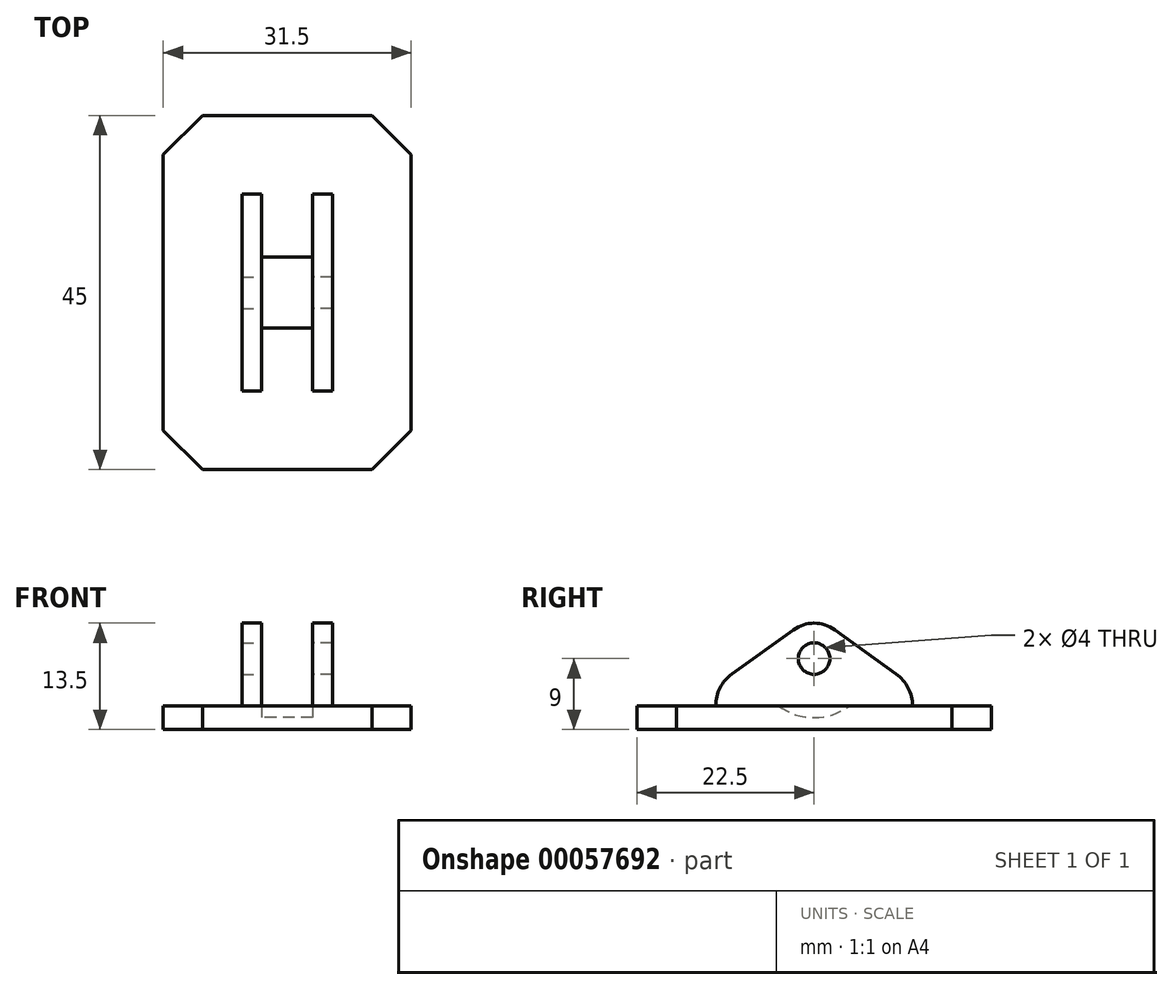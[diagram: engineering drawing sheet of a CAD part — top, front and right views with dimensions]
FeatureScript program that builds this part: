
annotation { "Feature Type Name" : "Feature", "Feature Type Description" : "" }
export const myFeature = defineFeature(function(context is Context, id is Id, definition is map)
    precondition{}
    {
        {
            var Q0;
            Q0=qCreatedBy(makeId("Right.planeOp"),FACE);
            var sketch = newSketch(context, id + "F0", { "sketchPlane" : qUnion([Q0])});
            skLineSegment(sketch, "E0", {"start": v(0, 0) * mm, "end": v(0, 6) * mm, "construction": true});
            skCircle(sketch, "E1", {"center": v(0, 6) * mm, "radius": 6.5 * mm, "construction": true});
            skCircle(sketch, "E2", {"center": v(0, 6) * mm, "radius": 2 * mm, "construction": true});
            skCircle(sketch, "E3", {"center": v(0, 6) * mm, "radius": 4.5 * mm, "construction": true});
            skLineSegment(sketch, "E4", {"start": v(-12.5, 0) * mm, "end": v(12.5, 0) * mm, "construction": true});
            skLineSegment(sketch, "E5", {"start": v(-12.5, -3) * mm, "end": v(-12.5, 0) * mm});
            skLineSegment(sketch, "E6", {"start": v(-12.5, -3) * mm, "end": v(12.5, -3) * mm});
            skLineSegment(sketch, "E7", {"start": v(12.5, 0) * mm, "end": v(12.5, -3) * mm});
            skArc(sketch, "E8", {"start": v(12.5, 0) * mm, "mid": v(11.95, 2.28) * mm, "end": v(10.42, 4.06) * mm, "construction": true});
            skLineSegment(sketch, "E9", {"start": v(2.62, 9.66) * mm, "end": v(10.42, 4.06) * mm, "construction": true});
            skLineSegment(sketch, "E10", {"start": v(4.5, 8.3) * mm, "end": v(4.5, 6) * mm, "construction": true});
            skLineSegment(sketch, "E11.MirrorCS", {"start": v(-2.62, 9.66) * mm, "end": v(-10.42, 4.06) * mm, "construction": true});
            skArc(sketch, "E12.MirrorCS", {"start": v(-12.5, 0) * mm, "mid": v(-11.95, 2.28) * mm, "end": v(-10.42, 4.06) * mm, "construction": true});
            skLineSegment(sketch, "E13.MirrorCS", {"start": v(-4.5, 8.3) * mm, "end": v(-4.5, 6) * mm, "construction": true});
            skPoint(sketch, "E14", {"position": v(0, -0.5) * mm});
            skArc(sketch, "E15", {"start": v(-2.5, 0) * mm, "mid": v(0, -0.5) * mm, "end": v(2.5, 0) * mm});
            skLineSegment(sketch, "E16", {"start": v(2.5, 0) * mm, "end": v(12.5, 0) * mm});
            skLineSegment(sketch, "E17", {"start": v(-2.5, 0) * mm, "end": v(-12.5, 0) * mm});
            skArc(sketch, "E18", {"start": v(-4.5, 0) * mm, "mid": v(0, -1.5) * mm, "end": v(4.5, 0) * mm});
            skSolve(sketch);
        }
        {
            var Q0;
            Q0=makeQuery(id+"F0.imprint","IMPRINT",FACE,{"disambiguationData":[TD([[makeQuery(id+"F0.imprint","IMPRINT",EDGE,{"derivedFrom":sQuery(id+"F0.wireOp",EDGE,"E5")}),-1.0]])]});
            extrude(context, id + "F1", {"entities" : qUnion([Q0]), "depth" : 3.25 * mm});
        }
        {
            var Q0;
            Q0=makeQuery(id+"F1.opExtrude","CAP_FACE",FACE,{"disambiguationData":[OSD([sQuery(id+"F0.wireOp",EDGE,"E5"),sQuery(id+"F0.wireOp",EDGE,"E6"),sQuery(id+"F0.wireOp",EDGE,"E7"),sQuery(id+"F0.wireOp",EDGE,"E15"),sQuery(id+"F0.wireOp",EDGE,"E16"),sQuery(id+"F0.wireOp",EDGE,"E17")])],"isStart":false});
            var sketch = newSketch(context, id + "F2", { "sketchPlane" : qUnion([Q0])});
            skLineSegment(sketch, "E19.0", {"start": v(-4.5, 8.3) * mm, "end": v(-10.42, 4.06) * mm});
            skArc(sketch, "E19.1", {"start": v(-12.5, 0) * mm, "mid": v(-11.95, 2.28) * mm, "end": v(-10.42, 4.06) * mm});
            skLineSegment(sketch, "E19.3", {"start": v(4.5, 8.3) * mm, "end": v(10.42, 4.06) * mm});
            skArc(sketch, "E19.4", {"start": v(12.5, 0) * mm, "mid": v(11.95, 2.28) * mm, "end": v(10.42, 4.06) * mm});
            skLineSegment(sketch, "E19.5", {"start": v(12.5, 0) * mm, "end": v(12.5, -3) * mm});
            skLineSegment(sketch, "E19.6", {"start": v(-12.5, -3) * mm, "end": v(12.5, -3) * mm});
            skLineSegment(sketch, "E19.7", {"start": v(-12.5, -3) * mm, "end": v(-12.5, 0) * mm});
            skPoint(sketch, "E20.orphan", {"position": v(-2.62, 9.66) * mm});
            skPoint(sketch, "E21.orphan", {"position": v(2.62, 9.66) * mm});
            skArc(sketch, "E22.0", {"start": v(-2, 6) * mm, "mid": v(0, 4) * mm, "end": v(2, 6) * mm});
            skLineSegment(sketch, "E23", {"start": v(-4.5, 8.3) * mm, "end": v(-2.62, 9.66) * mm});
            skLineSegment(sketch, "E24", {"start": v(4.5, 8.3) * mm, "end": v(2.62, 9.66) * mm});
            skPoint(sketch, "E25.start.orphan", {"position": v(4.5, 6) * mm});
            skPoint(sketch, "E19.2.end.orphan", {"position": v(-4.5, 6) * mm});
            skPoint(sketch, "E26.orphan", {"position": v(-1.11, 10.74) * mm});
            skPoint(sketch, "E27.orphan", {"position": v(1.11, 10.74) * mm});
            skCircle(sketch, "E28.0", {"center": v(0, 6) * mm, "radius": 2 * mm});
            skArc(sketch, "E29.0", {"start": v(2.62, 9.66) * mm, "mid": v(0, 10.5) * mm, "end": v(-2.62, 9.66) * mm});
            skSolve(sketch);
        }
        {
            var Q0;
            Q0 = qSketchRegion(id + "F2", true);
            extrude(context, id + "F3", {"entities" : qUnion([Q0]), "operationType" : NewBodyOperationType.ADD, "depth" : 2.5 * mm});
        }
        {
            var Q0;
            Q0=makeQuery(id+"F3.boolean.opBoolean","MERGE",FACE,{"derivedFrom":[makeQuery(id+"F1.opExtrude","SWEPT_FACE",FACE,{"disambiguationData":[OSD([sQuery(id+"F0.wireOp",EDGE,"E6")])]}),makeQuery(id+"F3.opExtrude","SWEPT_FACE",FACE,{"disambiguationData":[OSD([sQuery(id+"F2.wireOp",EDGE,"E19.6")])]})]});
            var sketch = newSketch(context, id + "F4", { "sketchPlane" : qUnion([Q0])});
            skLineSegment(sketch, "E30", {"start": v(0, -11.5) * mm, "end": v(0, -22.5) * mm});
            skLineSegment(sketch, "E31", {"start": v(0, -22.5) * mm, "end": v(10.75, -22.5) * mm});
            skLineSegment(sketch, "E32", {"start": v(10.75, -22.5) * mm, "end": v(15.75, -17.5) * mm});
            skLineSegment(sketch, "E33", {"start": v(15.75, -17.5) * mm, "end": v(15.75, 17.5) * mm});
            skLineSegment(sketch, "E34", {"start": v(10.75, 22.5) * mm, "end": v(15.75, 17.5) * mm});
            skLineSegment(sketch, "E35", {"start": v(10.75, 22.5) * mm, "end": v(0, 22.5) * mm});
            skLineSegment(sketch, "E36", {"start": v(0, 22.5) * mm, "end": v(0, 11.5) * mm});
            skLineSegment(sketch, "E37", {"start": v(0, 11.5) * mm, "end": v(4.75, 11.5) * mm});
            skLineSegment(sketch, "E38", {"start": v(4.75, 11.5) * mm, "end": v(4.75, -11.5) * mm});
            skLineSegment(sketch, "E39", {"start": v(4.75, -11.5) * mm, "end": v(0, -11.5) * mm});
            skSolve(sketch);
        }
        {
            var Q0;
            Q0 = qSketchRegion(id + "F4", true);
            var Q1;
            Q1=makeQuery(id+"F1.opExtrude","SWEPT_FACE",FACE,{"disambiguationData":[OSD([sQuery(id+"F0.wireOp",EDGE,"E16")])]});
            extrude(context, id + "F5", {"entities" : qUnion([Q0]), "operationType" : NewBodyOperationType.ADD, "endBound" : BoundingType.UP_TO_SURFACE, "oppositeDirection" : true, "endBoundEntityFace" : qUnion([Q1]), "depth" : 25 * mm});
        }
        {
            var Q0;
            Q0=makeQuery(id+"F1.opExtrude","SWEPT_BODY",BODY,{"disambiguationData":[OSD([sQuery(id+"F0.wireOp",EDGE,"E5"),sQuery(id+"F0.wireOp",EDGE,"E6"),sQuery(id+"F0.wireOp",EDGE,"E7"),sQuery(id+"F0.wireOp",EDGE,"E15"),sQuery(id+"F0.wireOp",EDGE,"E16"),sQuery(id+"F0.wireOp",EDGE,"E17")])]});
            var Q1;
            Q1=qCreatedBy(makeId("Right.planeOp"),FACE);
            mirror(context, id + "F6", {"operationType" : NewBodyOperationType.ADD, "entities" : qUnion([Q0]), "mirrorPlane" : qUnion([Q1])});
        }
    });
